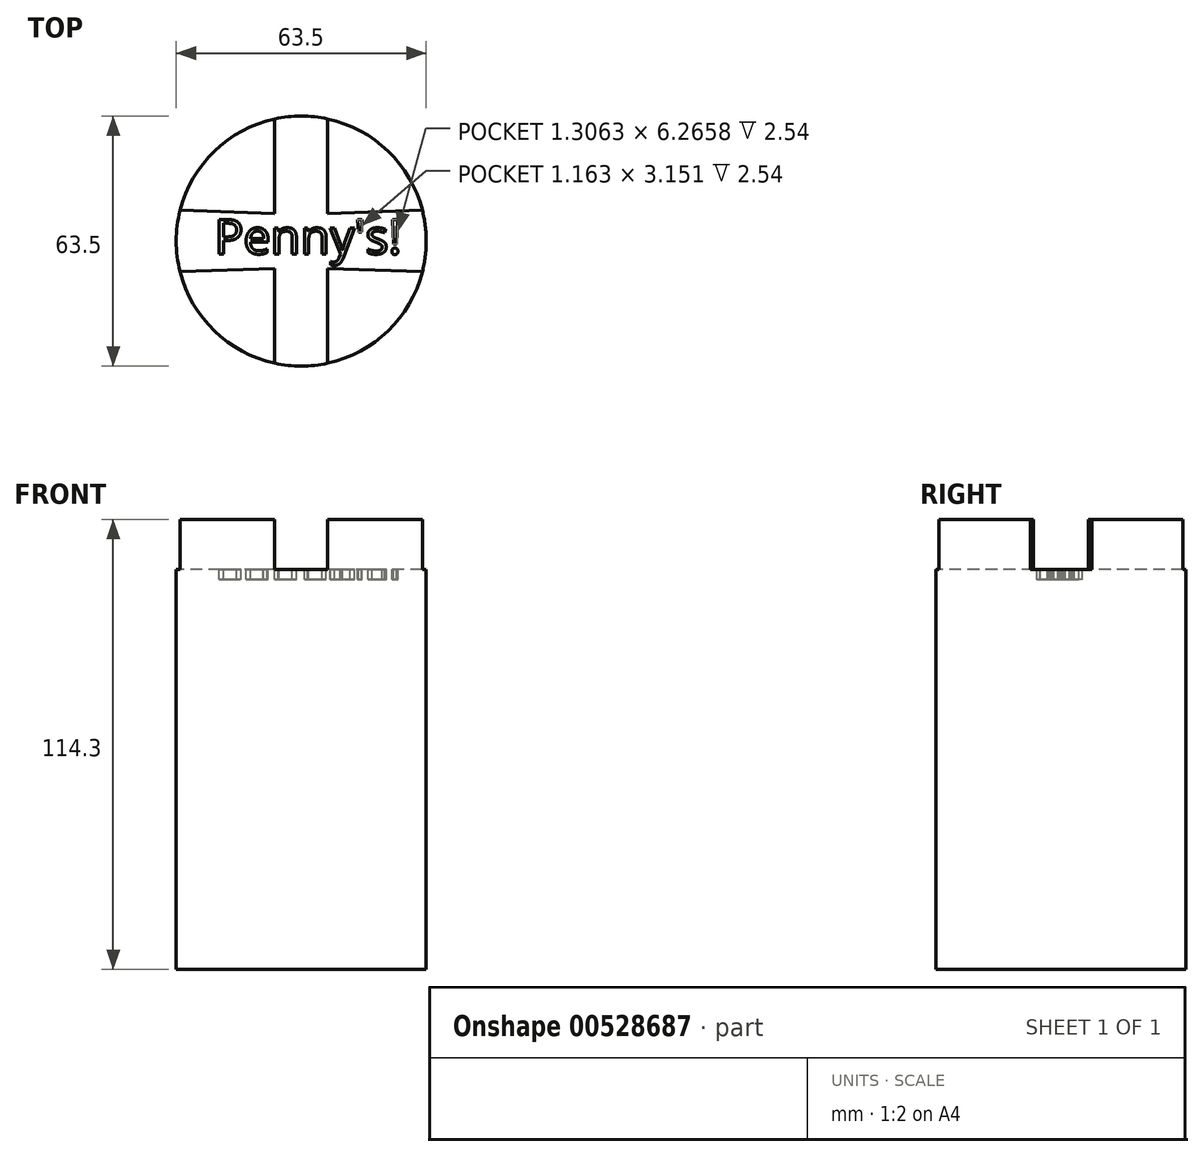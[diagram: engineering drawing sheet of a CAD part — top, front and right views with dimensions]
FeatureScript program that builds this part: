
annotation { "Feature Type Name" : "Feature", "Feature Type Description" : "" }
export const myFeature = defineFeature(function(context is Context, id is Id, definition is map)
    precondition{}
    {
        {
            var Q0;
            Q0=qCreatedBy(makeId("Top.planeOp"),FACE);
            var sketch = newSketch(context, id + "F0", { "sketchPlane" : qUnion([Q0])});
            skCircle(sketch, "E0", {"center": v(0, 0) * mm, "radius": 31.75 * mm});
            skSolve(sketch);
        }
        {
            var Q0;
            Q0=makeQuery(id+"F0.imprint","IMPRINT",FACE,{"disambiguationData":[TD([[makeQuery(id+"F0.imprint","IMPRINT",EDGE,{"derivedFrom":sQuery(id+"F0.wireOp",EDGE,"E0")}),1.0]])]});
            extrude(context, id + "F1", {"entities" : qUnion([Q0]), "oppositeDirection" : true, "depth" : 114.3 * mm, "offsetDistance" : 25.4 * mm});
        }
        {
            var Q0;
            Q0=makeQuery(id+"F1.opExtrude","CAP_FACE",FACE,{"disambiguationData":[OSD([sQuery(id+"F0.wireOp",EDGE,"E0")])],"isStart":true});
            var sketch = newSketch(context, id + "F2", { "sketchPlane" : qUnion([Q0])});
            skLineSegment(sketch, "E1.bottom", {"start": v(6.73, 38.1) * mm, "end": v(-6.73, 38.1) * mm});
            skLineSegment(sketch, "E1.top", {"start": v(6.73, -38.1) * mm, "end": v(-6.73, -38.1) * mm});
            skLineSegment(sketch, "E1.left", {"start": v(6.73, 38.1) * mm, "end": v(6.73, -38.1) * mm});
            skLineSegment(sketch, "E1.right", {"start": v(-6.73, 38.1) * mm, "end": v(-6.73, -38.1) * mm});
            skPoint(sketch, "E1.middle", {"position": v(0, 0) * mm});
            skLineSegment(sketch, "E2", {"start": v(0, 0) * mm, "end": v(28.95, 0) * mm, "construction": true});
            skLineSegment(sketch, "E3", {"start": v(0, 0) * mm, "end": v(0, 45.64) * mm, "construction": true});
            skPoint(sketch, "E3.endSnap0", {"position": v(0, 38.1) * mm});
            skLineSegment(sketch, "E4", {"start": v(0, 0) * mm, "end": v(28.84, 1) * mm, "construction": true});
            skSolve(sketch);
        }
        {
            var Q0;
            {var subQ0=sQuery(id+"F2.wireOp",EDGE,"E1.left");var subQ1=makeQuery(id+"F1.opExtrude","CAP_EDGE",EDGE,{"disambiguationData":[OSD([sQuery(id+"F0.wireOp",EDGE,"E0")])],"isStart":true});var subQ2=makeQuery(id+"F2.imprint","INTERSECT",VERTEX,{"disambiguationData":[OD(0.0)],"derivedFrom":[subQ1,subQ0]});Q0=makeQuery(id+"F2.imprint","IMPRINT",FACE,{"disambiguationData":[TD([[makeQuery(id+"F2.imprint","IMPRINT",EDGE,{"disambiguationData":[TD([[subQ2,-1.0]])],"derivedFrom":subQ0}),-1.0]])]});}
            extrude(context, id + "F3", {"entities" : qUnion([Q0]), "operationType" : NewBodyOperationType.REMOVE, "oppositeDirection" : true, "depth" : 12.7 * mm, "offsetDistance" : 25.4 * mm});
        }
        {
            var Q0;
            {var subQ0=sQuery(id+"F0.wireOp",EDGE,"E0");Q0=makeQuery(id+"F3.boolean.opBoolean","SPLIT",FACE,{"disambiguationData":[TD([makeQuery(id+"F3.opExtrude","SWEPT_FACE",FACE,{"disambiguationData":[OSD([sQuery(id+"F2.wireOp",EDGE,"E1.left")])]})])],"derivedFrom":makeQuery(id+"F1.opExtrude","CAP_FACE",FACE,{"disambiguationData":[OSD([subQ0])],"isStart":true})});}
            var sketch = newSketch(context, id + "F4", { "sketchPlane" : qUnion([Q0])});
            skLineSegment(sketch, "E5", {"start": v(0, 0) * mm, "end": v(80.2, 0) * mm, "construction": true});
            skLineSegment(sketch, "E6.bottom", {"start": v(51.61, 4.93) * mm, "end": v(-51.14, 8.52) * mm});
            skLineSegment(sketch, "E6.top", {"start": v(51.14, -8.52) * mm, "end": v(-51.61, -4.93) * mm});
            skLineSegment(sketch, "E6.left", {"start": v(51.61, 4.93) * mm, "end": v(51.14, -8.52) * mm});
            skLineSegment(sketch, "E6.right", {"start": v(-51.14, 8.52) * mm, "end": v(-51.61, -4.93) * mm});
            skPoint(sketch, "E6.middle", {"position": v(0, 0) * mm});
            skLineSegment(sketch, "E7.bottom", {"start": v(41.98, 8.2) * mm, "end": v(-42.45, 5.25) * mm});
            skLineSegment(sketch, "E7.top", {"start": v(42.45, -5.25) * mm, "end": v(-41.98, -8.2) * mm});
            skLineSegment(sketch, "E7.left", {"start": v(41.98, 8.2) * mm, "end": v(42.45, -5.25) * mm});
            skLineSegment(sketch, "E7.right", {"start": v(-42.45, 5.25) * mm, "end": v(-41.98, -8.2) * mm});
            skSolve(sketch);
        }
        {
            var Q0;
            {var subQ1=sQuery(id+"F4.wireOp",EDGE,"E7.bottom");var subQ3=sQuery(id+"F4.wireOp",EDGE,"E6.bottom");var subQ4=makeQuery(id+"F4.imprint","INTERSECT",VERTEX,{"derivedFrom":[subQ3,subQ1]});Q0=makeQuery(id+"F4.imprint","IMPRINT",FACE,{"disambiguationData":[TD([[makeQuery(id+"F4.imprint","IMPRINT",EDGE,{"disambiguationData":[TD([[subQ4,1.0]])],"derivedFrom":subQ3}),1.0]])]});}
            var Q1;
            {var subQ0=sQuery(id+"F4.wireOp",EDGE,"E7.top");var subQ1=sQuery(id+"F4.wireOp",EDGE,"E6.top");var subQ2=makeQuery(id+"F4.imprint","INTERSECT",VERTEX,{"derivedFrom":[subQ1,subQ0]});Q1=makeQuery(id+"F4.imprint","IMPRINT",FACE,{"disambiguationData":[TD([[makeQuery(id+"F4.imprint","IMPRINT",EDGE,{"disambiguationData":[TD([[subQ2,-1.0]])],"derivedFrom":subQ1}),1.0]])]});}
            var Q2;
            {var subQ5=sQuery(id+"F4.wireOp",EDGE,"E6.right");Q2=makeQuery(id+"F4.imprint","IMPRINT",FACE,{"disambiguationData":[TD([[makeQuery(id+"F4.imprint","IMPRINT",EDGE,{"derivedFrom":subQ5}),1.0]])]});}
            var Q3;
            {var subQ0=sQuery(id+"F4.wireOp",EDGE,"E6.bottom");var subQ2=sQuery(id+"F2.wireOp",EDGE,"E1.left");var subQ5=makeQuery(id+"F3.boolean.opBoolean","COPY",EDGE,{"derivedFrom":makeQuery(id+"F3.opExtrude","CAP_EDGE",EDGE,{"disambiguationData":[OSD([subQ2])],"isStart":true})});var subQ6=makeQuery(id+"F4.imprint","INTERSECT",VERTEX,{"derivedFrom":[subQ5,subQ0]});Q3=makeQuery(id+"F4.imprint","IMPRINT",FACE,{"disambiguationData":[TD([[makeQuery(id+"F4.imprint","IMPRINT",EDGE,{"disambiguationData":[TD([[subQ6,-1.0]])],"derivedFrom":subQ5}),1.0]])]});}
            var Q4;
            {var subQ2=sQuery(id+"F2.wireOp",EDGE,"E1.left");var subQ5=makeQuery(id+"F3.boolean.opBoolean","COPY",EDGE,{"derivedFrom":makeQuery(id+"F3.opExtrude","CAP_EDGE",EDGE,{"disambiguationData":[OSD([subQ2])],"isStart":true})});var subQ7=sQuery(id+"F4.wireOp",EDGE,"E7.bottom");var subQ9=makeQuery(id+"F4.imprint","INTERSECT",VERTEX,{"derivedFrom":[subQ5,subQ7]});Q4=makeQuery(id+"F4.imprint","IMPRINT",FACE,{"disambiguationData":[TD([[makeQuery(id+"F4.imprint","IMPRINT",EDGE,{"disambiguationData":[TD([[subQ9,-1.0]])],"derivedFrom":subQ5}),1.0]])]});}
            var Q5;
            {var subQ0=sQuery(id+"F4.wireOp",EDGE,"E6.top");var subQ2=sQuery(id+"F2.wireOp",EDGE,"E1.left");var subQ5=makeQuery(id+"F3.boolean.opBoolean","COPY",EDGE,{"derivedFrom":makeQuery(id+"F3.opExtrude","CAP_EDGE",EDGE,{"disambiguationData":[OSD([subQ2])],"isStart":true})});var subQ6=makeQuery(id+"F4.imprint","INTERSECT",VERTEX,{"derivedFrom":[subQ5,subQ0]});Q5=makeQuery(id+"F4.imprint","IMPRINT",FACE,{"disambiguationData":[TD([[makeQuery(id+"F4.imprint","IMPRINT",EDGE,{"disambiguationData":[TD([[subQ6,1.0]])],"derivedFrom":subQ5}),1.0]])]});}
            extrude(context, id + "F5", {"entities" : qUnion([Q0, Q1, Q2, Q3, Q4, Q5]), "operationType" : NewBodyOperationType.REMOVE, "oppositeDirection" : true, "depth" : 12.7 * mm, "offsetDistance" : 25.4 * mm});
        }
        {
            var Q0;
            {var subQ0=sQuery(id+"F2.wireOp",EDGE,"E1.left");var subQ1=sQuery(id+"F0.wireOp",EDGE,"E0");Q0=makeQuery(id+"F5.boolean.opBoolean","MERGE",FACE,{"derivedFrom":[makeQuery(id+"F3.boolean.opBoolean","COPY",FACE,{"derivedFrom":makeQuery(id+"F3.opExtrude","CAP_FACE",FACE,{"disambiguationData":[OSD([subQ1,subQ0,sQuery(id+"F2.wireOp",EDGE,"E1.right")])],"isStart":false})}),makeQuery(id+"F5.opExtrude","CAP_FACE",FACE,{"disambiguationData":[OSD([subQ1,subQ0,sQuery(id+"F4.wireOp",EDGE,"E6.bottom"),sQuery(id+"F4.wireOp",EDGE,"E6.top"),sQuery(id+"F4.wireOp",EDGE,"E6.right"),sQuery(id+"F4.wireOp",EDGE,"E7.bottom"),sQuery(id+"F4.wireOp",EDGE,"E7.top"),sQuery(id+"F4.wireOp",EDGE,"E7.right")])],"isStart":false})]});}
            var sketch = newSketch(context, id + "F6", { "sketchPlane" : qUnion([Q0])});
            skText(sketch, "E8", { "text": "Penny\'s!", "fontName": "NotoSans-Regular.ttf"});
            const initialGuessF6  = {"E8": [-0.02207, -0.00327, 1, 0, 0.0088]};
            skSetInitialGuess(sketch, initialGuessF6);
            skSolve(sketch);
        }
        {
            var Q0;
            Q0 = qSketchRegion(id + "F6", true);
            extrude(context, id + "F7", {"entities" : qUnion([Q0]), "operationType" : NewBodyOperationType.REMOVE, "oppositeDirection" : true, "depth" : 2.54 * mm, "offsetDistance" : 25.4 * mm});
        }
    });
